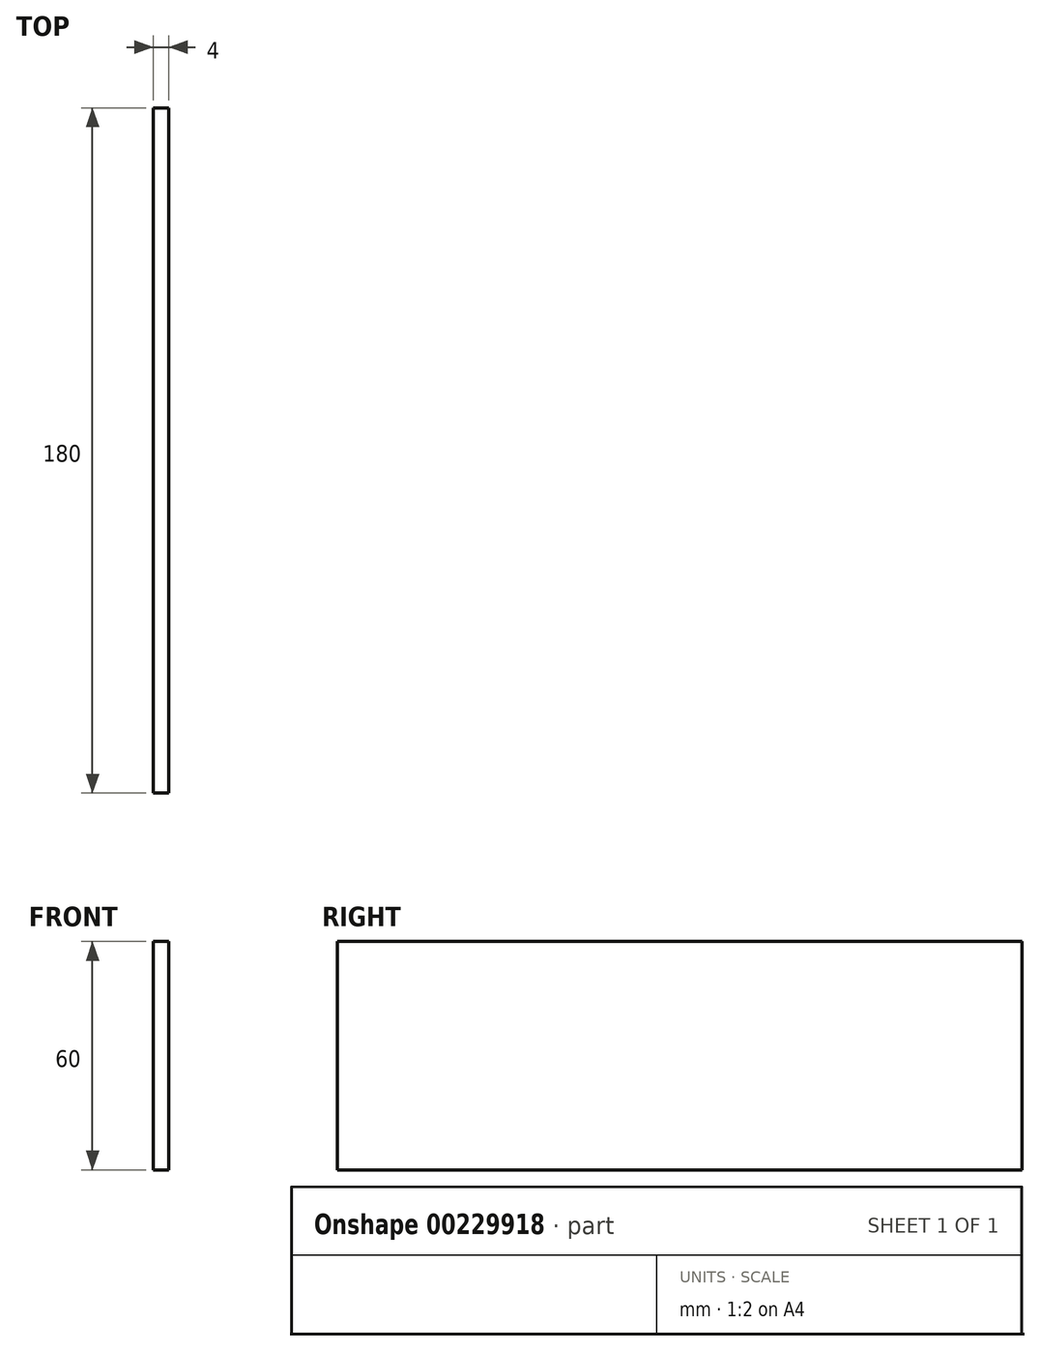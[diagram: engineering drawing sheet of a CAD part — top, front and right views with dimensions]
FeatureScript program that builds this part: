
annotation { "Feature Type Name" : "Feature", "Feature Type Description" : "" }
export const myFeature = defineFeature(function(context is Context, id is Id, definition is map)
    precondition{}
    {
        {
            var Q0;
            Q0=qCreatedBy(makeId("Right.planeOp"),FACE);
            var sketch = newSketch(context, id + "F0", { "sketchPlane" : qUnion([Q0])});
            skLineSegment(sketch, "E0.bottom", {"start": v(0, 2.67) * mm, "end": v(180, 2.67) * mm});
            skLineSegment(sketch, "E0.top", {"start": v(0, 62.67) * mm, "end": v(180, 62.67) * mm});
            skLineSegment(sketch, "E0.left", {"start": v(0, 2.67) * mm, "end": v(0, 62.67) * mm});
            skLineSegment(sketch, "E0.right", {"start": v(180, 2.67) * mm, "end": v(180, 62.67) * mm});
            skSolve(sketch);
        }
        {
            var Q0;
            Q0=makeQuery(id+"F0.imprint","IMPRINT",FACE,{"disambiguationData":[TD([[makeQuery(id+"F0.imprint","IMPRINT",EDGE,{"derivedFrom":sQuery(id+"F0.wireOp",EDGE,"E0.bottom")}),1.0]])]});
            extrude(context, id + "F1", {"entities" : qUnion([Q0]), "oppositeDirection" : true, "depth" : 4 * mm});
        }
    });
